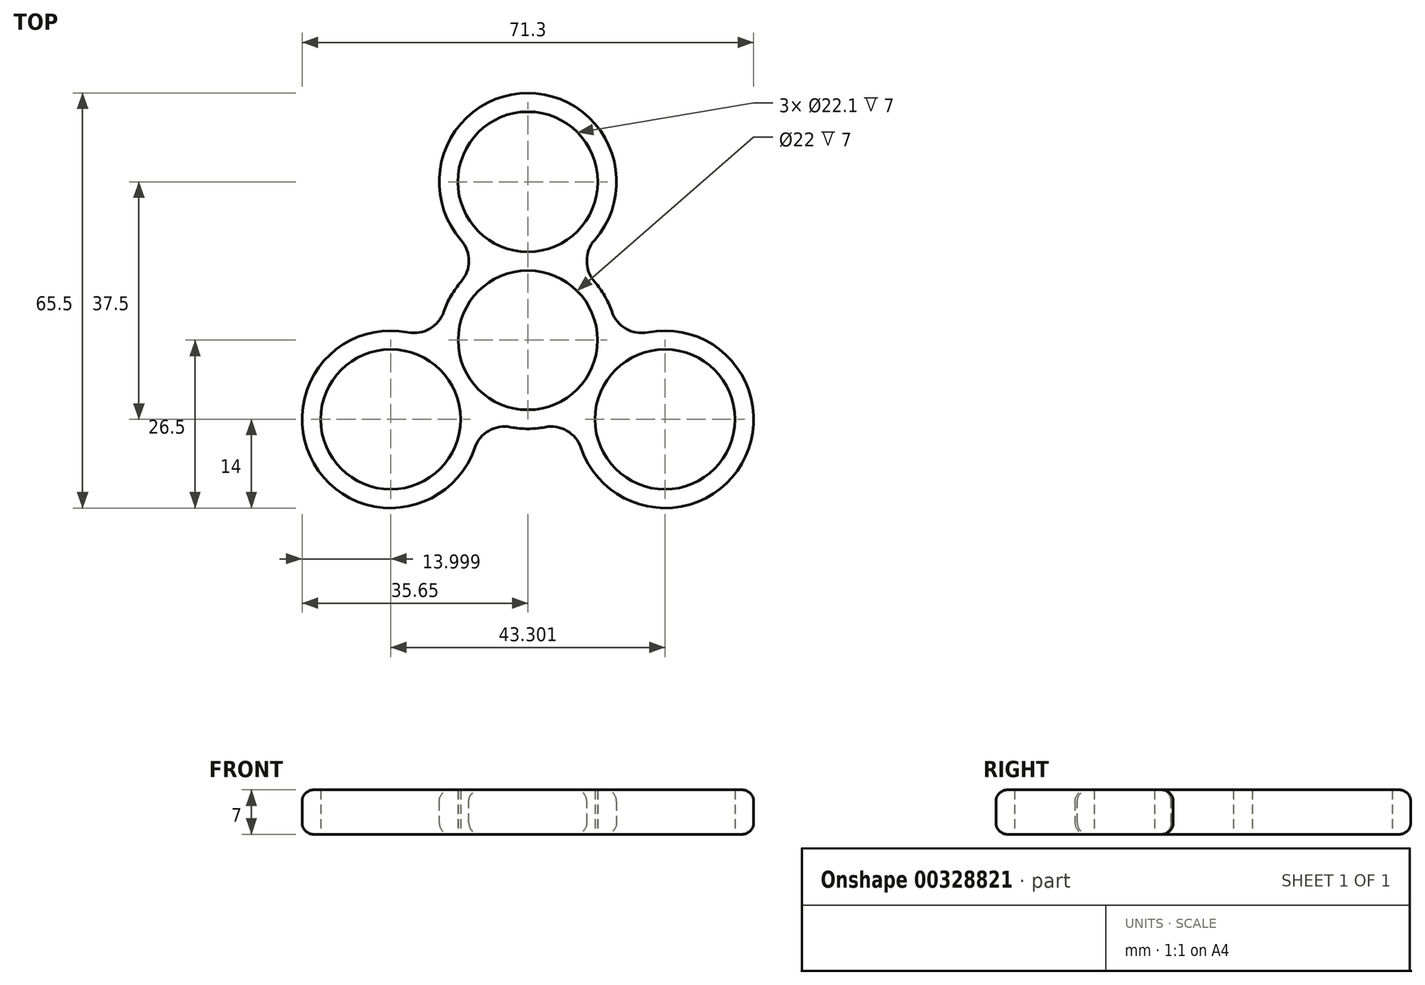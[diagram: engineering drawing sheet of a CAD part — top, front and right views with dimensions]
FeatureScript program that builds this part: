
annotation { "Feature Type Name" : "Feature", "Feature Type Description" : "" }
export const myFeature = defineFeature(function(context is Context, id is Id, definition is map)
    precondition{}
    {
        {
            var Q0;
            Q0=qCreatedBy(makeId("Top.planeOp"),FACE);
            var sketch = newSketch(context, id + "F0", { "sketchPlane" : qUnion([Q0])});
            skCircle(sketch, "E0", {"center": v(0, 0) * mm, "radius": 11 * mm});
            skCircle(sketch, "E1", {"center": v(0, 25) * mm, "radius": 11.05 * mm});
            skCircle(sketch, "E2.1.0", {"center": v(-21.65, -12.5) * mm, "radius": 11.05 * mm});
            skCircle(sketch, "E2.2.0", {"center": v(21.65, -12.5) * mm, "radius": 11.05 * mm});
            skArc(sketch, "E3", {"start": v(-6.3, 12.5) * mm, "mid": v(-12.12, 7) * mm, "end": v(-13.98, -0.79) * mm});
            skArc(sketch, "E4", {"start": v(6.3, 12.5) * mm, "mid": v(0, 39) * mm, "end": v(-6.3, 12.5) * mm});
            skArc(sketch, "E5.1.0", {"start": v(-13.98, -0.79) * mm, "mid": v(-33.77, -19.5) * mm, "end": v(-7.67, -11.71) * mm});
            skArc(sketch, "E5.2.0", {"start": v(7.67, -11.71) * mm, "mid": v(33.77, -19.5) * mm, "end": v(13.98, -0.79) * mm});
            skArc(sketch, "E6.trimOffspring", {"start": v(-7.67, -11.71) * mm, "mid": v(0, -14) * mm, "end": v(7.67, -11.71) * mm});
            skArc(sketch, "E7.trimOffspring", {"start": v(13.98, -0.79) * mm, "mid": v(12.12, 7) * mm, "end": v(6.3, 12.5) * mm});
            skSolve(sketch);
        }
        {
            var Q0;
            Q0=makeQuery(id+"F0.imprint","IMPRINT",FACE,{"disambiguationData":[TD([[makeQuery(id+"F0.imprint","IMPRINT",EDGE,{"derivedFrom":sQuery(id+"F0.wireOp",EDGE,"E0")}),-1.0]])]});
            extrude(context, id + "F1", {"entities" : qUnion([Q0]), "depth" : 7 * mm});
        }
        {
            var Q0;
            Q0=makeQuery(id+"F1.opExtrude","SWEPT_EDGE",EDGE,{"disambiguationData":[OSD([sQuery(id+"F0.wireOp",EDGE,"E5.1.0"),sQuery(id+"F0.wireOp",EDGE,"E6.trimOffspring")])]});
            var Q1;
            Q1=makeQuery(id+"F1.opExtrude","SWEPT_EDGE",EDGE,{"disambiguationData":[OSD([sQuery(id+"F0.wireOp",EDGE,"E5.2.0"),sQuery(id+"F0.wireOp",EDGE,"E6.trimOffspring")])]});
            var Q2;
            Q2=makeQuery(id+"F1.opExtrude","SWEPT_EDGE",EDGE,{"disambiguationData":[OSD([sQuery(id+"F0.wireOp",EDGE,"E5.2.0"),sQuery(id+"F0.wireOp",EDGE,"E7.trimOffspring")])]});
            var Q3;
            Q3=makeQuery(id+"F1.opExtrude","SWEPT_EDGE",EDGE,{"disambiguationData":[OSD([sQuery(id+"F0.wireOp",EDGE,"E4"),sQuery(id+"F0.wireOp",EDGE,"E7.trimOffspring")])]});
            var Q4;
            Q4=makeQuery(id+"F1.opExtrude","SWEPT_EDGE",EDGE,{"disambiguationData":[OSD([sQuery(id+"F0.wireOp",EDGE,"E3"),sQuery(id+"F0.wireOp",EDGE,"E4")])]});
            var Q5;
            Q5=makeQuery(id+"F1.opExtrude","SWEPT_EDGE",EDGE,{"disambiguationData":[OSD([sQuery(id+"F0.wireOp",EDGE,"E3"),sQuery(id+"F0.wireOp",EDGE,"E5.1.0")])]});
            fillet(context, id + "F2", {"entities" : qUnion([Q0, Q1, Q2, Q3, Q4, Q5]), "radius" : 5 * mm, "tangentPropagation" : true, "allowEdgeOverflow" : false});
        }
        {
            var Q0;
            Q0=makeQuery(id+"F1.opExtrude","CAP_EDGE",EDGE,{"disambiguationData":[OSD([sQuery(id+"F0.wireOp",EDGE,"E4")])],"isStart":false});
            var Q1;
            Q1=makeQuery(id+"F1.opExtrude","CAP_EDGE",EDGE,{"disambiguationData":[OSD([sQuery(id+"F0.wireOp",EDGE,"E4")])],"isStart":true});
            fillet(context, id + "F3", {"entities" : qUnion([Q0, Q1]), "radius" : 1.8 * mm, "tangentPropagation" : true, "allowEdgeOverflow" : false});
        }
    });
